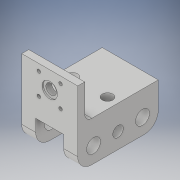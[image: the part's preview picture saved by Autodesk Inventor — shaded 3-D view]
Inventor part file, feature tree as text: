
AUTODESK INVENTOR PART (.ipt)
format: ipt  version: 2019 (Build 230136000, 136)  size: 209,920 bytes
history: native  units: mm
features: sketch x6, extrude x5, hole x4, fillet x2
ambient origin geometry x8: Origin, YZ Plane, XZ Plane, XY Plane, X Axis, Y Axis, Z Axis, Center Point
bodies: Solid1 (feature_tree)
feature tree (17):
  extrude  "Extrusion1"  Depth=80.0mm
  extrude  "Extrusion11"  Depth=20.0mm
  sketch  "Sketch13"  dims[d57=115.0mm d58=37.5mm d59=0.0mm]
  hole  "Hole2"  [1 undecoded]
  hole  "Hole3"  [1 undecoded]
  hole  "Hole6"  [1 undecoded]
  fillet  "Fillet19"  Radius=10.0mm
  extrude  "Extrusion15"  Depth=10.0mm TaperAngle=0.0deg
  sketch  "Sketch21"  dims[d112=25.0mm d113=15.0mm d114=6.0mm d115=4.0mm d116=2.0mm d117=90.0deg d118=15.0mm d119=0.0mm d120=20.0mm d122=10.0mm d123=50.0mm d124=0.0mm d126=50.0mm d127=0.0mm d128=15.0mm d129=35.0mm d130=35.0mm d131=15.0mm d132=25.0mm d133=10.0mm d134=15.5mm d135=15.5mm d136=40.0mm d138=360.0deg d140=5.0mm d141=6.0mm d142=4.0mm d143=2.0mm d144=90.0deg d145=15.0mm d146=0.0mm d147=22.0mm d148=2.0mm d149=0.0mm d12=1.0mm d13=1.0mm d14=1.0mm d15=0.15mm d16=0.25mm d17=0.375mm d18=14.3117mm d19=0.75mm d20=20.594885mm d21=0.0625mm d22=0.75mm d23=0.375mm]
  extrude  "Extrusion16"  Depth=10.0mm TaperAngle=0.0deg
  fillet  "Fillet20"  Radius=15.0mm
  hole  "Hole7"  [1 undecoded]
  extrude  "Extrusion17"  Depth=10.0mm
  sketch  "Sketch1"  dims[d0=115.0mm d1=80.0mm]
  sketch  "Sketch12"  dims[d2=20.0mm d3=0.0mm d56=20.0mm]
  sketch  "Sketch19"  dims[d63=20.0mm d64=6.0mm d65=4.0mm d66=2.0mm d67=90.0deg d68=8.0mm d69=20.594885mm]
  sketch  "Sketch20"  dims[d70=15.0mm d71=6.0mm d72=4.0mm d73=2.0mm d74=90.0deg d75=8.0mm d76=20.594885mm d111=25.0mm]
note: 4 required parameter values undecoded (feature->parameter linkage not recoverable at this tier; creation-order binding heuristic only, values carry confidence <= 0.55)
